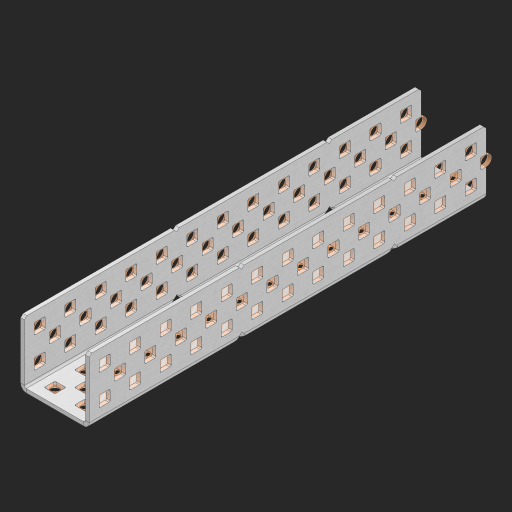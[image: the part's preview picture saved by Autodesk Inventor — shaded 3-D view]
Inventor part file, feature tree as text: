
AUTODESK INVENTOR PART (.ipt)
format: ipt  version: 2023 (Build 270158000, 158)  size: 1,660,928 bytes
history: native  units: in
note: dims shown in document units (in); Inventor stores cm internally (conversion verified against a paired STEP export)
features: other x162, extrude x154, sheet_metal_op x8, sketch x7, mirror x3, pattern_linear x2, chamfer x1
ambient origin geometry x8: Origin, YZ Plane, XZ Plane, XY Plane, X Axis, Y Axis, Z Axis, Center Point
bodies: Solid1 (feature_tree), Body (feature_tree)
feature tree (337):
  sheet_metal_op  "Flanges"
  sheet_metal_op  "Body Pattern"
  pattern_linear  "Center Pattern"  Spacing1=1.0in  [1 undecoded]
  other  "Arc Length"
  mirror  "Notch Mirror"
  pattern_linear  "Notch Pattern"  Spacing1=0.25in  [1 undecoded]
  other  "Diagonal Plane"
  mirror  "Flange 1"
  mirror  "Flange 2"
  chamfer  "End Chamfer"
  sketch  "Sketch1"  dims[d0=1.0in]
  other  "Plate1"
  sketch  "Sketch2"  dims[d1=6.5in]
  other  "Plate2"
  sheet_metal_op  "Bend1"
  sheet_metal_op  "Corner1"
  sketch  "Sketch8"  dims[d2=0.0625in]
  sketch  "Sketch9"  dims[d3=0.0625in]
  other  "Srf91"
  sheet_metal_op  "Body Pattern Sketch"
  other  "Srf92"
  sketch  "Sketch13"  dims[d4=0.0312in]
  sketch  "Sketch15"  dims[d5=0.125in]
  sketch  "Sketch16"  dims[d6=0.0625in d7=1.0in d8=90.0deg d9=0.0312in d10=0.25in d11=0.0625in d12=0.0625in d49=0.182in d50=0.02in d52=0.25in d53=0.0625in d54=0.0in d55=0.172in d56=1.0in d57=0.0in d60=5.1181in d62=0.5in d63=0.7874in d65=0.5in d85=0.1473in d86=0.1782in d88=0.04in d89=0.0625in d90=0.0in d91=0.04in d92=0.0491in d95=2.5in d96=0.04in d97=0.25in d98=45.0deg d99=0.25in d102=2.497in d106=0.182in d107=0.02in d108=0.5in d110=0.0625in d111=0.0in d112=0.172in d113=0.5in d114=0.0in d117=0.5in d118=0.5in d131=0.25in d132=0.25in]
  other  "Srf786"
  other  "Srf889"
  other  "Srf890"
  other  "Srf891"
  other  "Srf892"
  other  "Srf893"
  other  "Srf894"
  other  "Srf895"
  other  "Srf896"
  other  "Srf996"
  other  "Srf997"
  other  "Srf998"
  other  "Srf999"
  other  "Srf1315"
  other  "Srf1316"
  other  "Srf1317"
  other  "Srf1325"
  other  "Srf1326"
  other  "Srf1327"
  other  "Srf1328"
  other  "Srf1329"
  other  "Srf1330"
  other  "Srf1331"
  other  "Srf1332"
  other  "Srf1338"
  other  "Srf1339"
  other  "Srf1340"
  other  "Srf1341"
  other  "Srf1374"
  other  "Srf1375"
  other  "Srf1376"
  other  "Srf1384"
  other  "Srf1385"
  other  "Srf1386"
  other  "Srf1387"
  other  "Srf1388"
  other  "Srf1389"
  other  "Srf1390"
  other  "Srf1391"
  other  "Srf1397"
  other  "Srf1398"
  other  "Srf1399"
  other  "Srf1400"
  other  "Srf1433"
  other  "Srf1434"
  other  "Srf1473"
  other  "Srf1474"
  other  "Srf1475"
  other  "Srf1476"
  other  "Srf1477"
  other  "Srf1478"
  other  "Srf1479"
  other  "Srf1480"
  other  "Srf1481"
  other  "Srf1482"
  other  "Srf1483"
  other  "Srf1484"
  other  "Srf1485"
  other  "Srf1500"
  other  "Srf1501"
  other  "Srf1502"
  other  "Srf1503"
  other  "Srf1504"
  other  "Srf1505"
  other  "Srf1506"
  other  "Srf1507"
  other  "Srf1508"
  other  "Srf1509"
  other  "Srf1510"
  other  "Srf1511"
  other  "Srf1512"
  other  "Srf1513"
  other  "Srf1514"
  other  "Srf1515"
  other  "Srf1516"
  other  "Srf1517"
  other  "Srf1518"
  other  "Srf1519"
  other  "Srf1520"
  other  "Srf1521"
  other  "Srf1522"
  other  "Srf1523"
  other  "Srf1538"
  other  "Srf1539"
  other  "Srf1540"
  other  "Srf1541"
  other  "Srf1542"
  other  "Srf1543"
  other  "Srf1544"
  other  "Srf1545"
  other  "Srf1546"
  other  "Srf1547"
  other  "Srf1548"
  other  "Srf1549"
  other  "Srf1550"
  other  "Srf1551"
  other  "Srf1552"
  other  "Srf1553"
  other  "Srf1554"
  other  "Srf1555"
  other  "Srf1556"
  other  "Srf1557"
  other  "Srf1558"
  other  "Srf1559"
  other  "Srf1560"
  other  "Srf1561"
  other  "Srf1576"
  other  "Srf1577"
  other  "Srf1578"
  other  "Srf1579"
  other  "Srf1580"
  other  "Srf1581"
  other  "Srf1582"
  other  "Srf1583"
  other  "Srf1584"
  other  "Srf1585"
  other  "Srf1586"
  other  "Srf1587"
  other  "Srf1588"
  other  "Srf1589"
  other  "Srf1590"
  other  "Srf1591"
  other  "Srf1592"
  other  "Srf1593"
  other  "Srf1594"
  other  "Srf1595"
  other  "Srf1596"
  other  "Srf1597"
  other  "Srf1598"
  other  "Srf1599"
  other  "Srf1614"
  other  "Srf1615"
  other  "Srf1616"
  other  "Srf1617"
  other  "Srf1618"
  other  "Srf1619"
  other  "Srf1620"
  other  "Srf1621"
  other  "Srf1622"
  other  "Srf1623"
  other  "Srf1624"
  other  "Srf1625"
  other  "Srf1626"
  other  "Srf1627"
  other  "Srf1628"
  other  "Srf1629"
  other  "Srf1630"
  other  "Srf1631"
  other  "Srf1632"
  other  "Srf1633"
  other  "Srf1634"
  other  "Srf1635"
  other  "Srf1636"
  other  "Srf1637"
  sheet_metal_op  "Body Stamp"
  sheet_metal_op  "Body Circle"
  other  "Center Stamp"
  other  "Center Circle"
  sheet_metal_op  "Notch"
  extrude  "ExtrusionSrf92"  Depth=0.0625in
  extrude  "ExtrusionSrf889"  Depth=0.0625in
  extrude  "ExtrusionSrf890"  Depth=0.182in
  extrude  "ExtrusionSrf891"  Depth=0.02in
  extrude  "ExtrusionSrf892"  Depth=0.25in
  extrude  "ExtrusionSrf893"  Depth=0.0625in
  extrude  "ExtrusionSrf894"  TaperAngle=0.0deg  [1 undecoded]
  extrude  "ExtrusionSrf895"  Depth=0.25in
  extrude  "ExtrusionSrf896"  Depth=1.0in TaperAngle=0.0deg
  extrude  "ExtrusionSrf996"  Depth=0.25in
  extrude  "ExtrusionSrf997"  Depth=0.5in
  extrude  "ExtrusionSrf998"  Depth=0.25in
  extrude  "ExtrusionSrf999"  Depth=0.25in
  extrude  "ExtrusionSrf1315"  Depth=0.25in
  extrude  "ExtrusionSrf1316"  Depth=0.0625in
  extrude  "ExtrusionSrf1355"  TaperAngle=0.0deg  [1 undecoded]
  extrude  "ExtrusionSrf1356"  Depth=0.25in
  extrude  "ExtrusionSrf1357"  Depth=0.25in
  extrude  "ExtrusionSrf1358"  Depth=2.5in
  extrude  "ExtrusionSrf1359"  Depth=0.25in TaperAngle=45.0deg
  extrude  "ExtrusionSrf1360"  Depth=0.25in
  extrude  "ExtrusionSrf1361"  Depth=0.25in
  extrude  "ExtrusionSrf1362"  Depth=0.182in
  extrude  "ExtrusionSrf1363"  Depth=0.02in
  extrude  "ExtrusionSrf1364"  Depth=0.5in
  extrude  "ExtrusionSrf1365"  Depth=0.0625in
  extrude  "ExtrusionSrf1366"  TaperAngle=0.0deg  [1 undecoded]
  extrude  "ExtrusionSrf1367"  Depth=0.25in
  extrude  "ExtrusionSrf1374"  Depth=0.5in TaperAngle=0.0deg
  extrude  "ExtrusionSrf1375"  Depth=0.5in
  extrude  "ExtrusionSrf1414"  Depth=0.5in
  extrude  "ExtrusionSrf1415"  Depth=0.25in
  extrude  "ExtrusionSrf1416"  Depth=0.25in
  extrude  "ExtrusionSrf1417"  [1 undecoded]
  extrude  "ExtrusionSrf1418"  [1 undecoded]
  extrude  "ExtrusionSrf1419"  [1 undecoded]
  extrude  "ExtrusionSrf1420"  [1 undecoded]
  extrude  "ExtrusionSrf1421"  [1 undecoded]
  extrude  "ExtrusionSrf1422"  [1 undecoded]
  extrude  "ExtrusionSrf1423"  [1 undecoded]
  extrude  "ExtrusionSrf1424"  [1 undecoded]
  extrude  "ExtrusionSrf1425"  [1 undecoded]
  extrude  "ExtrusionSrf1426"  [1 undecoded]
  extrude  "ExtrusionSrf1433"  [1 undecoded]
  extrude  "ExtrusionSrf1434"  [1 undecoded]
  extrude  "ExtrusionSrf1473"  [1 undecoded]
  extrude  "ExtrusionSrf1474"  [1 undecoded]
  extrude  "ExtrusionSrf1475"  [1 undecoded]
  extrude  "ExtrusionSrf1476"  [1 undecoded]
  extrude  "ExtrusionSrf1477"  [1 undecoded]
  extrude  "ExtrusionSrf1478"  [1 undecoded]
  extrude  "ExtrusionSrf1479"  [1 undecoded]
  extrude  "ExtrusionSrf1480"  [1 undecoded]
  extrude  "ExtrusionSrf1481"  [1 undecoded]
  extrude  "ExtrusionSrf1482"  [1 undecoded]
  extrude  "ExtrusionSrf1483"  [1 undecoded]
  extrude  "ExtrusionSrf1484"  [1 undecoded]
  extrude  "ExtrusionSrf1485"  [1 undecoded]
  extrude  "ExtrusionSrf1500"  [1 undecoded]
  extrude  "ExtrusionSrf1501"  [1 undecoded]
  extrude  "ExtrusionSrf1502"  [1 undecoded]
  extrude  "ExtrusionSrf1503"  [1 undecoded]
  extrude  "ExtrusionSrf1504"  [1 undecoded]
  extrude  "ExtrusionSrf1505"  [1 undecoded]
  extrude  "ExtrusionSrf1506"  [1 undecoded]
  extrude  "ExtrusionSrf1507"  [1 undecoded]
  extrude  "ExtrusionSrf1508"  [1 undecoded]
  extrude  "ExtrusionSrf1509"  [1 undecoded]
  extrude  "ExtrusionSrf1510"  [1 undecoded]
  extrude  "ExtrusionSrf1511"  [1 undecoded]
  extrude  "ExtrusionSrf1512"  [1 undecoded]
  extrude  "ExtrusionSrf1513"  [1 undecoded]
  extrude  "ExtrusionSrf1514"  [1 undecoded]
  extrude  "ExtrusionSrf1515"  [1 undecoded]
  extrude  "ExtrusionSrf1516"  [1 undecoded]
  extrude  "ExtrusionSrf1517"  [1 undecoded]
  extrude  "ExtrusionSrf1518"  [1 undecoded]
  extrude  "ExtrusionSrf1519"  [1 undecoded]
  extrude  "ExtrusionSrf1520"  [1 undecoded]
  extrude  "ExtrusionSrf1521"  [1 undecoded]
  extrude  "ExtrusionSrf1522"  [1 undecoded]
  extrude  "ExtrusionSrf1523"  [1 undecoded]
  extrude  "ExtrusionSrf1538"  [1 undecoded]
  extrude  "ExtrusionSrf1539"  [1 undecoded]
  extrude  "ExtrusionSrf1540"  [1 undecoded]
  extrude  "ExtrusionSrf1541"  [1 undecoded]
  extrude  "ExtrusionSrf1542"  [1 undecoded]
  extrude  "ExtrusionSrf1543"  [1 undecoded]
  extrude  "ExtrusionSrf1544"  [1 undecoded]
  extrude  "ExtrusionSrf1545"  [1 undecoded]
  extrude  "ExtrusionSrf1546"  [1 undecoded]
  extrude  "ExtrusionSrf1547"  [1 undecoded]
  extrude  "ExtrusionSrf1548"  [1 undecoded]
  extrude  "ExtrusionSrf1549"  [1 undecoded]
  extrude  "ExtrusionSrf1550"  [1 undecoded]
  extrude  "ExtrusionSrf1551"  [1 undecoded]
  extrude  "ExtrusionSrf1552"  [1 undecoded]
  extrude  "ExtrusionSrf1553"  [1 undecoded]
  extrude  "ExtrusionSrf1554"  [1 undecoded]
  extrude  "ExtrusionSrf1555"  [1 undecoded]
  extrude  "ExtrusionSrf1556"  [1 undecoded]
  extrude  "ExtrusionSrf1557"  [1 undecoded]
  extrude  "ExtrusionSrf1558"  [1 undecoded]
  extrude  "ExtrusionSrf1559"  [1 undecoded]
  extrude  "ExtrusionSrf1560"  [1 undecoded]
  extrude  "ExtrusionSrf1561"  [1 undecoded]
  extrude  "ExtrusionSrf1576"  [1 undecoded]
  extrude  "ExtrusionSrf1577"  [1 undecoded]
  extrude  "ExtrusionSrf1578"  [1 undecoded]
  extrude  "ExtrusionSrf1579"  [1 undecoded]
  extrude  "ExtrusionSrf1580"  [1 undecoded]
  extrude  "ExtrusionSrf1581"  [1 undecoded]
  extrude  "ExtrusionSrf1582"  [1 undecoded]
  extrude  "ExtrusionSrf1583"  [1 undecoded]
  extrude  "ExtrusionSrf1584"  [1 undecoded]
  extrude  "ExtrusionSrf1585"  [1 undecoded]
  extrude  "ExtrusionSrf1586"  [1 undecoded]
  extrude  "ExtrusionSrf1587"  [1 undecoded]
  extrude  "ExtrusionSrf1588"  [1 undecoded]
  extrude  "ExtrusionSrf1589"  [1 undecoded]
  extrude  "ExtrusionSrf1590"  [1 undecoded]
  extrude  "ExtrusionSrf1591"  [1 undecoded]
  extrude  "ExtrusionSrf1592"  [1 undecoded]
  extrude  "ExtrusionSrf1593"  [1 undecoded]
  extrude  "ExtrusionSrf1594"  [1 undecoded]
  extrude  "ExtrusionSrf1595"  [1 undecoded]
  extrude  "ExtrusionSrf1596"  [1 undecoded]
  extrude  "ExtrusionSrf1597"  [1 undecoded]
  extrude  "ExtrusionSrf1598"  [1 undecoded]
  extrude  "ExtrusionSrf1599"  [1 undecoded]
  extrude  "ExtrusionSrf1614"  [1 undecoded]
  extrude  "ExtrusionSrf1615"  [1 undecoded]
  extrude  "ExtrusionSrf1616"  [1 undecoded]
  extrude  "ExtrusionSrf1617"  [1 undecoded]
  extrude  "ExtrusionSrf1618"  [1 undecoded]
  extrude  "ExtrusionSrf1619"  [1 undecoded]
  extrude  "ExtrusionSrf1620"  [1 undecoded]
  extrude  "ExtrusionSrf1621"  [1 undecoded]
  extrude  "ExtrusionSrf1622"  [1 undecoded]
  extrude  "ExtrusionSrf1623"  [1 undecoded]
  extrude  "ExtrusionSrf1624"  [1 undecoded]
  extrude  "ExtrusionSrf1625"  [1 undecoded]
  extrude  "ExtrusionSrf1626"  [1 undecoded]
  extrude  "ExtrusionSrf1627"  [1 undecoded]
  extrude  "ExtrusionSrf1628"  [1 undecoded]
  extrude  "ExtrusionSrf1629"  [1 undecoded]
  extrude  "ExtrusionSrf1630"  [1 undecoded]
  extrude  "ExtrusionSrf1631"  [1 undecoded]
  extrude  "ExtrusionSrf1632"  [1 undecoded]
  extrude  "ExtrusionSrf1633"  [1 undecoded]
  extrude  "ExtrusionSrf1634"  [1 undecoded]
  extrude  "ExtrusionSrf1635"  [1 undecoded]
  extrude  "ExtrusionSrf1636"  [1 undecoded]
  extrude  "ExtrusionSrf1637"  [1 undecoded]
note: 126 required parameter values undecoded (feature->parameter linkage not recoverable at this tier; creation-order binding heuristic only, values carry confidence <= 0.55)
